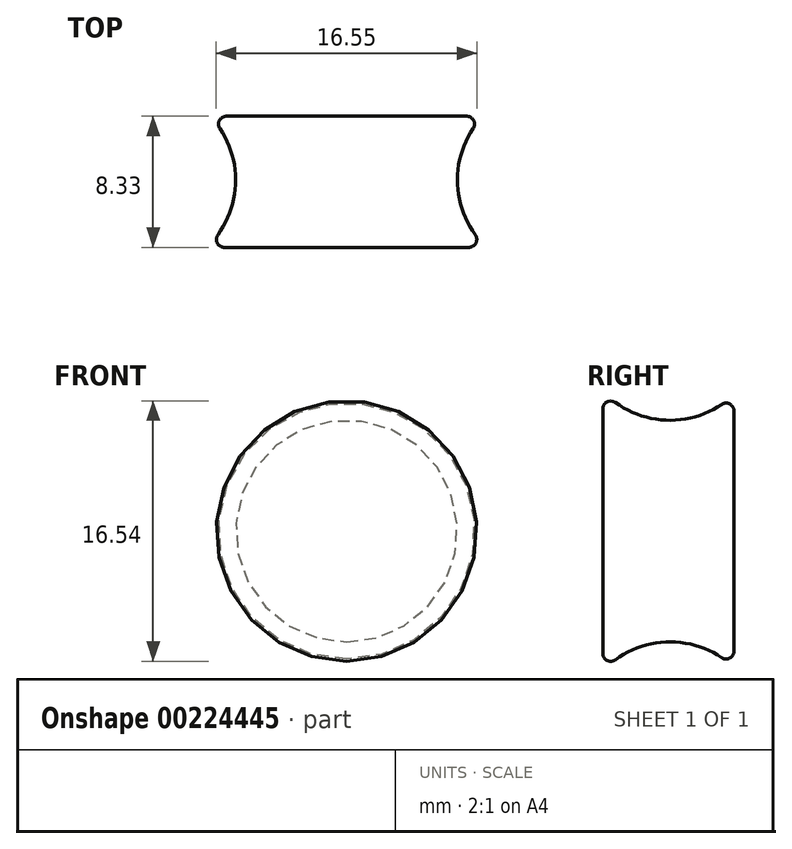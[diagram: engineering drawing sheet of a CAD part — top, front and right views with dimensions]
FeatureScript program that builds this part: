
annotation { "Feature Type Name" : "Feature", "Feature Type Description" : "" }
export const myFeature = defineFeature(function(context is Context, id is Id, definition is map)
    precondition{}
    {
        {
            var Q0;
            Q0=qCreatedBy(makeId("Top.planeOp"),FACE);
            var sketch = newSketch(context, id + "F0", { "sketchPlane" : qUnion([Q0])});
            skCircle(sketch, "E0", {"center": v(-65.1, -20.83) * mm, "radius": 8.88 * mm});
            skCircle(sketch, "E1", {"center": v(-65.1, -20.83) * mm, "radius": 6.9 * mm});
            skLineSegment(sketch, "E2.bottom", {"start": v(-65.1, -20.83) * mm, "end": v(-67.06, -20.83) * mm});
            skLineSegment(sketch, "E2.top", {"start": v(-65.1, -19.35) * mm, "end": v(-67.06, -19.35) * mm});
            skLineSegment(sketch, "E2.left", {"start": v(-65.1, -20.83) * mm, "end": v(-65.1, -19.35) * mm});
            skLineSegment(sketch, "E2.right", {"start": v(-67.06, -20.83) * mm, "end": v(-67.06, -19.35) * mm});
            skLineSegment(sketch, "E3", {"start": v(-50.18, -40.4) * mm, "end": v(-32.43, -40.4) * mm});
            skLineSegment(sketch, "E4", {"start": v(-41.3, -40.4) * mm, "end": v(-41.3, -32.07) * mm});
            skLineSegment(sketch, "E5", {"start": v(-50.18, -32.07) * mm, "end": v(-32.63, -32.07) * mm});
            skLineSegment(sketch, "E6", {"start": v(-32.43, -40.4) * mm, "end": v(-32.63, -32.07) * mm});
            skLineSegment(sketch, "E7", {"start": v(-50.18, -40.4) * mm, "end": v(-50.18, -32.07) * mm});
            skLineSegment(sketch, "E8", {"start": v(-41.3, -36.23) * mm, "end": v(-48.35, -36.23) * mm});
            skLineSegment(sketch, "E9", {"start": v(-41.3, -36.23) * mm, "end": v(-34.27, -36.23) * mm});
            skArc(sketch, "E10", {"start": v(-32.63, -32.07) * mm, "mid": v(-34.26, -36.27) * mm, "end": v(-32.43, -40.4) * mm});
            skArc(sketch, "E11", {"start": v(-50.18, -40.4) * mm, "mid": v(-48.35, -36.23) * mm, "end": v(-50.18, -32.07) * mm});
            skSolve(sketch);
        }
        {
            var Q0;
            {var subQ5=sQuery(id+"F0.wireOp",EDGE,"E9");Q0=makeQuery(id+"F0.imprint","IMPRINT",FACE,{"disambiguationData":[TD([[makeQuery(id+"F0.imprint","IMPRINT",EDGE,{"derivedFrom":subQ5}),-1.0]])]});}
            var Q1;
            {var subQ3=sQuery(id+"F0.wireOp",EDGE,"E9");Q1=makeQuery(id+"F0.imprint","IMPRINT",FACE,{"disambiguationData":[TD([[makeQuery(id+"F0.imprint","IMPRINT",EDGE,{"derivedFrom":subQ3}),1.0]])]});}
            var Q2;
            Q2=sQuery(id+"F0.wireOp",EDGE,"E4");
            revolve(context, id + "F1", {"entities" : qUnion([Q0, Q1]), "axis" : qUnion([Q2]), "revolveType" : RevolveType.FULL});
        }
        {
            var Q0;
            Q0=makeQuery(id+"F1.opRevolve","SWEPT_EDGE",EDGE,{"disambiguationData":[OSD([sQuery(id+"F0.wireOp",EDGE,"E3"),sQuery(id+"F0.wireOp",EDGE,"E6"),sQuery(id+"F0.wireOp",EDGE,"E10")])]});
            var Q1;
            Q1=makeQuery(id+"F1.opRevolve","SWEPT_EDGE",EDGE,{"disambiguationData":[OSD([sQuery(id+"F0.wireOp",EDGE,"E5"),sQuery(id+"F0.wireOp",EDGE,"E6"),sQuery(id+"F0.wireOp",EDGE,"E10")])]});
            fillet(context, id + "F2", {"entities" : qUnion([Q0, Q1]), "radius" : .5 * mm, "tangentPropagation" : true, "allowEdgeOverflow" : false});
        }
    });
